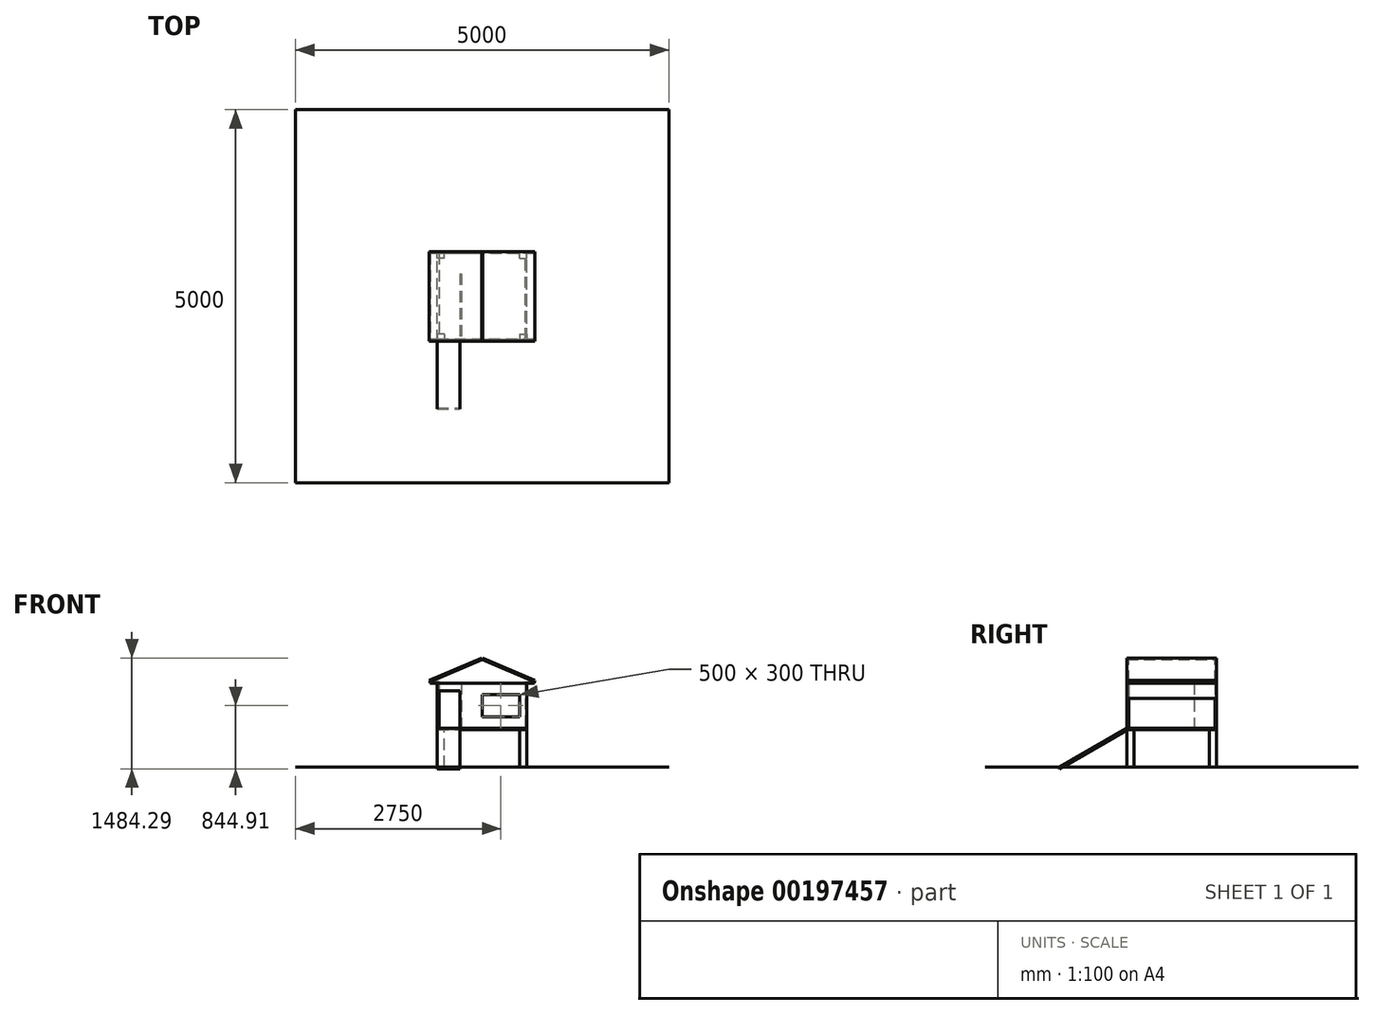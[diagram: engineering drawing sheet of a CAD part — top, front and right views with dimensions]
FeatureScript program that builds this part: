
annotation { "Feature Type Name" : "Feature", "Feature Type Description" : "" }
export const myFeature = defineFeature(function(context is Context, id is Id, definition is map)
    precondition{}
    {
        {
            var Q0;
            Q0=qCreatedBy(makeId("Top.planeOp"),FACE);
            var sketch = newSketch(context, id + "F0", { "sketchPlane" : qUnion([Q0])});
            skLineSegment(sketch, "E0.bottom", {"start": v(2500, -2500) * mm, "end": v(-2500, -2500) * mm});
            skLineSegment(sketch, "E0.top", {"start": v(2500, 2500) * mm, "end": v(-2500, 2500) * mm});
            skLineSegment(sketch, "E0.left", {"start": v(2500, -2500) * mm, "end": v(2500, 2500) * mm});
            skLineSegment(sketch, "E0.right", {"start": v(-2500, -2500) * mm, "end": v(-2500, 2500) * mm});
            skPoint(sketch, "E0.middle", {"position": v(0, 0) * mm});
            skSolve(sketch);
        }
        {
            var Q0;
            Q0 = qSketchRegion(id + "F0", true);
            extrude(context, id + "F1", {"entities" : qUnion([Q0]), "oppositeDirection" : true, "depth" : 1 * mm});
        }
        {
            var Q0;
            Q0=qCreatedBy(makeId("Top.planeOp"),FACE);
            cPlane(context, id + "F2", {"entities" : qUnion([Q0]), "cplaneType" : CPlaneType.OFFSET, "offset" : 500 * mm, "width" : 150 * mm, "height" : 150 * mm});
        }
        {
            var Q0;
            Q0=qCreatedBy(id+"F2.planeOp",FACE);
            var sketch = newSketch(context, id + "F3", { "sketchPlane" : qUnion([Q0])});
            skLineSegment(sketch, "E1.bottom", {"start": v(600, -600) * mm, "end": v(-600, -600) * mm});
            skLineSegment(sketch, "E1.top", {"start": v(600, 600) * mm, "end": v(-600, 600) * mm});
            skLineSegment(sketch, "E1.left", {"start": v(600, -600) * mm, "end": v(600, 600) * mm});
            skLineSegment(sketch, "E1.right", {"start": v(-600, -600) * mm, "end": v(-600, 600) * mm});
            skPoint(sketch, "E1.middle", {"position": v(0, 0) * mm});
            skSolve(sketch);
        }
        {
            var Q0;
            Q0 = qSketchRegion(id + "F3", true);
            extrude(context, id + "F4", {"entities" : qUnion([Q0]), "depth" : 22 * mm});
        }
        {
            var Q0;
            Q0=qCreatedBy(id+"F2.planeOp",FACE);
            var sketch = newSketch(context, id + "F5", { "sketchPlane" : qUnion([Q0])});
            skLineSegment(sketch, "E2.bottom", {"start": v(-600, 600) * mm, "end": v(-505, 600) * mm});
            skLineSegment(sketch, "E2.top", {"start": v(-600, 505) * mm, "end": v(-505, 505) * mm});
            skLineSegment(sketch, "E2.left", {"start": v(-600, 600) * mm, "end": v(-600, 505) * mm});
            skLineSegment(sketch, "E2.right", {"start": v(-505, 600) * mm, "end": v(-505, 505) * mm});
            skLineSegment(sketch, "E3", {"start": v(0, 0) * mm, "end": v(0, 720.23) * mm, "construction": true});
            skLineSegment(sketch, "E4", {"start": v(-681.79, 0) * mm, "end": v(744.72, 0) * mm, "construction": true});
            skLineSegment(sketch, "E5.MirrorCS", {"start": v(505, 600) * mm, "end": v(505, 505) * mm});
            skLineSegment(sketch, "E6.MirrorCS", {"start": v(600, 600) * mm, "end": v(600, 505) * mm});
            skLineSegment(sketch, "E7.MirrorCS", {"start": v(600, 505) * mm, "end": v(505, 505) * mm});
            skLineSegment(sketch, "E8.MirrorCS", {"start": v(600, 600) * mm, "end": v(505, 600) * mm});
            skLineSegment(sketch, "E9.MirrorCS", {"start": v(-505, -600) * mm, "end": v(-505, -505) * mm});
            skLineSegment(sketch, "E10.MirrorCS", {"start": v(-600, -600) * mm, "end": v(-600, -505) * mm});
            skLineSegment(sketch, "E11.MirrorCS", {"start": v(-600, -505) * mm, "end": v(-505, -505) * mm});
            skLineSegment(sketch, "E12.MirrorCS", {"start": v(-600, -600) * mm, "end": v(-505, -600) * mm});
            skLineSegment(sketch, "E13.MirrorCS", {"start": v(505, -600) * mm, "end": v(505, -505) * mm});
            skLineSegment(sketch, "E14.MirrorCS", {"start": v(600, -600) * mm, "end": v(600, -505) * mm});
            skLineSegment(sketch, "E15.MirrorCS", {"start": v(600, -505) * mm, "end": v(505, -505) * mm});
            skLineSegment(sketch, "E16.MirrorCS", {"start": v(600, -600) * mm, "end": v(505, -600) * mm});
            skSolve(sketch);
        }
        {
            var Q0;
            Q0 = qSketchRegion(id + "F5", true);
            extrude(context, id + "F6", {"entities" : qUnion([Q0]), "endBound" : BoundingType.UP_TO_NEXT, "oppositeDirection" : true, "depth" : 25 * mm});
        }
        {
            var Q0;
            Q0=makeQuery(id+"F4.opExtrude","CAP_FACE",FACE,{"disambiguationData":[OSD([sQuery(id+"F3.wireOp",EDGE,"E1.bottom"),sQuery(id+"F3.wireOp",EDGE,"E1.top"),sQuery(id+"F3.wireOp",EDGE,"E1.left"),sQuery(id+"F3.wireOp",EDGE,"E1.right")])],"isStart":false});
            var sketch = newSketch(context, id + "F7", { "sketchPlane" : qUnion([Q0])});
            skLineSegment(sketch, "E17.bottom", {"start": v(-600, 600) * mm, "end": v(600, 600) * mm});
            skLineSegment(sketch, "E17.top", {"start": v(-600, -600) * mm, "end": v(600, -600) * mm});
            skLineSegment(sketch, "E17.left", {"start": v(-600, 600) * mm, "end": v(-600, -600) * mm});
            skLineSegment(sketch, "E17.right", {"start": v(600, 600) * mm, "end": v(600, -600) * mm});
            skLineSegment(sketch, "E18.0", {"start": v(-578, 578) * mm, "end": v(578, 578) * mm});
            skLineSegment(sketch, "E18.1", {"start": v(-578, 578) * mm, "end": v(-578, -578) * mm});
            skLineSegment(sketch, "E18.2", {"start": v(-578, -578) * mm, "end": v(578, -578) * mm});
            skLineSegment(sketch, "E18.3", {"start": v(578, 578) * mm, "end": v(578, -578) * mm});
            skSolve(sketch);
        }
        {
            var Q0;
            Q0 = qSketchRegion(id + "F7", true);
            extrude(context, id + "F8", {"entities" : qUnion([Q0]), "depth" : 600 * mm});
        }
        {
            var Q0;
            Q0=makeQuery(id+"F4.opExtrude","CAP_EDGE",EDGE,{"disambiguationData":[OSD([sQuery(id+"F3.wireOp",EDGE,"E1.bottom")])],"isStart":false});
            cPlane(context, id + "F9", {"entities" : qUnion([Q0]), "cplaneType" : CPlaneType.LINE_ANGLE, "offset" : 25 * mm, "angle" : 60 * degree, "width" : 150 * mm, "height" : 150 * mm});
        }
        {
            var Q0;
            Q0=qCreatedBy(id+"F9.planeOp",FACE);
            var sketch = newSketch(context, id + "F10", { "sketchPlane" : qUnion([Q0])});
            skLineSegment(sketch, "E19.bottom", {"start": v(-600, -258.62) * mm, "end": v(-300, -258.62) * mm});
            skLineSegment(sketch, "E19.top", {"start": v(-600, -1310.34) * mm, "end": v(-300, -1310.34) * mm});
            skLineSegment(sketch, "E19.left", {"start": v(-600, -258.62) * mm, "end": v(-600, -1310.34) * mm});
            skLineSegment(sketch, "E19.right", {"start": v(-300, -258.62) * mm, "end": v(-300, -1310.34) * mm});
            skSolve(sketch);
        }
        {
            var Q0;
            Q0 = qSketchRegion(id + "F10", true);
            extrude(context, id + "F11", {"entities" : qUnion([Q0]), "oppositeDirection" : true, "depth" : 22 * mm});
        }
        {
            var Q0;
            Q0=makeQuery(id+"F4.opExtrude","CAP_FACE",FACE,{"disambiguationData":[OSD([sQuery(id+"F3.wireOp",EDGE,"E1.bottom"),sQuery(id+"F3.wireOp",EDGE,"E1.top"),sQuery(id+"F3.wireOp",EDGE,"E1.left"),sQuery(id+"F3.wireOp",EDGE,"E1.right")])],"isStart":false});
            var sketch = newSketch(context, id + "F12", { "sketchPlane" : qUnion([Q0])});
            skLineSegment(sketch, "E20.bottom", {"start": v(-300, 300) * mm, "end": v(-278, 300) * mm});
            skLineSegment(sketch, "E20.top", {"start": v(-300, -578) * mm, "end": v(-278, -578) * mm});
            skLineSegment(sketch, "E20.left", {"start": v(-300, 300) * mm, "end": v(-300, -578) * mm});
            skLineSegment(sketch, "E20.right", {"start": v(-278, 300) * mm, "end": v(-278, -578) * mm});
            skSolve(sketch);
        }
        {
            var Q0;
            Q0 = qSketchRegion(id + "F12", true);
            extrude(context, id + "F13", {"entities" : qUnion([Q0]), "depth" : 600 * mm});
        }
        {
            var Q0;
            Q0=makeQuery(id+"F8.opExtrude","SWEPT_FACE",FACE,{"disambiguationData":[OSD([sQuery(id+"F7.wireOp",EDGE,"E17.top")])]});
            var sketch = newSketch(context, id + "F14", { "sketchPlane" : qUnion([Q0])});
            skLineSegment(sketch, "E21.bottom", {"start": v(-578, 1022) * mm, "end": v(-300, 1022) * mm});
            skLineSegment(sketch, "E21.top", {"start": v(-578, 522) * mm, "end": v(-300, 522) * mm});
            skLineSegment(sketch, "E21.left", {"start": v(-578, 1022) * mm, "end": v(-578, 522) * mm});
            skLineSegment(sketch, "E21.right", {"start": v(-300, 1022) * mm, "end": v(-300, 522) * mm});
            skSolve(sketch);
        }
        {
            var Q0;
            Q0 = qSketchRegion(id + "F14", true);
            extrude(context, id + "F15", {"entities" : qUnion([Q0]), "operationType" : NewBodyOperationType.REMOVE, "endBound" : BoundingType.UP_TO_NEXT, "oppositeDirection" : true, "depth" : 25 * mm});
        }
        {
            var Q0;
            Q0=makeQuery(id+"F8.opExtrude","SWEPT_FACE",FACE,{"disambiguationData":[OSD([sQuery(id+"F7.wireOp",EDGE,"E17.right")])]});
            var sketch = newSketch(context, id + "F16", { "sketchPlane" : qUnion([Q0])});
            skLineSegment(sketch, "E22.bottom", {"start": v(-578, 922) * mm, "end": v(578, 922) * mm});
            skLineSegment(sketch, "E22.top", {"start": v(-578, 522) * mm, "end": v(578, 522) * mm});
            skLineSegment(sketch, "E22.left", {"start": v(-578, 922) * mm, "end": v(-578, 522) * mm});
            skLineSegment(sketch, "E22.right", {"start": v(578, 922) * mm, "end": v(578, 522) * mm});
            skSolve(sketch);
        }
        {
            var Q0;
            Q0 = qSketchRegion(id + "F16", true);
            extrude(context, id + "F17", {"entities" : qUnion([Q0]), "operationType" : NewBodyOperationType.REMOVE, "endBound" : BoundingType.UP_TO_NEXT, "oppositeDirection" : true, "depth" : 25 * mm});
        }
        {
            var Q0;
            Q0=makeQuery(id+"F8.opExtrude","SWEPT_FACE",FACE,{"disambiguationData":[OSD([sQuery(id+"F7.wireOp",EDGE,"E17.right")])]});
            var sketch = newSketch(context, id + "F18", { "sketchPlane" : qUnion([Q0])});
            skLineSegment(sketch, "E23.bottom", {"start": v(-578, 922) * mm, "end": v(578, 922) * mm});
            skLineSegment(sketch, "E23.top", {"start": v(-578, 522) * mm, "end": v(578, 522) * mm});
            skLineSegment(sketch, "E23.left", {"start": v(-578, 922) * mm, "end": v(-578, 522) * mm});
            skLineSegment(sketch, "E23.right", {"start": v(578, 922) * mm, "end": v(578, 522) * mm});
            skSolve(sketch);
        }
        {
            var Q0;
            Q0 = qSketchRegion(id + "F18", true);
            extrude(context, id + "F19", {"entities" : qUnion([Q0]), "oppositeDirection" : true, "depth" : 22 * mm});
        }
        {
            var Q0;
            Q0=makeQuery(id+"F8.opExtrude","SWEPT_FACE",FACE,{"disambiguationData":[OSD([sQuery(id+"F7.wireOp",EDGE,"E17.top")])]});
            var sketch = newSketch(context, id + "F20", { "sketchPlane" : qUnion([Q0])});
            skLineSegment(sketch, "E24.bottom", {"start": v(0, 972) * mm, "end": v(500, 972) * mm});
            skLineSegment(sketch, "E24.top", {"start": v(0, 672) * mm, "end": v(500, 672) * mm});
            skLineSegment(sketch, "E24.left", {"start": v(0, 972) * mm, "end": v(0, 672) * mm});
            skLineSegment(sketch, "E24.right", {"start": v(500, 972) * mm, "end": v(500, 672) * mm});
            skSolve(sketch);
        }
        {
            var Q0;
            Q0 = qSketchRegion(id + "F20", true);
            extrude(context, id + "F21", {"entities" : qUnion([Q0]), "operationType" : NewBodyOperationType.REMOVE, "endBound" : BoundingType.UP_TO_NEXT, "oppositeDirection" : true, "depth" : 25 * mm});
        }
        {
            var Q0;
            Q0=makeQuery(id+"F8.opExtrude","SWEPT_FACE",FACE,{"disambiguationData":[OSD([sQuery(id+"F7.wireOp",EDGE,"E17.top")])]});
            var sketch = newSketch(context, id + "F22", { "sketchPlane" : qUnion([Q0])});
            skLineSegment(sketch, "E25", {"start": v(0, 0) * mm, "end": v(0, 1688.78) * mm, "construction": true});
            skLineSegment(sketch, "E26", {"start": v(-700, 1122) * mm, "end": v(700, 1122) * mm});
            skLineSegment(sketch, "E27", {"start": v(-700, 1122) * mm, "end": v(-700, 1144) * mm});
            skLineSegment(sketch, "E28", {"start": v(-700, 1144) * mm, "end": v(0, 1441.13) * mm});
            skLineSegment(sketch, "E29", {"start": v(700, 1122) * mm, "end": v(700, 1144) * mm});
            skLineSegment(sketch, "E30", {"start": v(700, 1144) * mm, "end": v(0, 1441.13) * mm});
            skSolve(sketch);
        }
        {
            var Q0;
            Q0 = qSketchRegion(id + "F22", true);
            extrude(context, id + "F23", {"entities" : qUnion([Q0]), "oppositeDirection" : true, "depth" : 22 * mm});
        }
        {
            var Q0;
            Q0=makeQuery(id+"F23.opExtrude","SWEPT_BODY",BODY,{"disambiguationData":[OSD([sQuery(id+"F22.wireOp",EDGE,"E26"),sQuery(id+"F22.wireOp",EDGE,"lWtLeS8S-gMhO-y6JL-Wjuz-mZaUUvy0QFBU"),sQuery(id+"F22.wireOp",EDGE,"m84qWRCe-eZef-hMwX-0Vxn-EiRq6ELt9xTd")])]});
            var Q1;
            Q1=qCreatedBy(makeId("Front.planeOp"),FACE);
            mirror(context, id + "F24", {"entities" : qUnion([Q0]), "mirrorPlane" : qUnion([Q1])});
        }
        {
            var Q0;
            Q0=makeQuery(id+"F8.opExtrude","CAP_FACE",FACE,{"disambiguationData":[OSD([sQuery(id+"F7.wireOp",EDGE,"E17.bottom"),sQuery(id+"F7.wireOp",EDGE,"E17.top"),sQuery(id+"F7.wireOp",EDGE,"E17.left"),sQuery(id+"F7.wireOp",EDGE,"E17.right"),sQuery(id+"F7.wireOp",EDGE,"E18.0"),sQuery(id+"F7.wireOp",EDGE,"E18.1"),sQuery(id+"F7.wireOp",EDGE,"E18.2"),sQuery(id+"F7.wireOp",EDGE,"E18.3")])],"isStart":false});
            var sketch = newSketch(context, id + "F25", { "sketchPlane" : qUnion([Q0])});
            skLineSegment(sketch, "E31.bottom", {"start": v(-578, 578) * mm, "end": v(-700, 578) * mm});
            skLineSegment(sketch, "E31.top", {"start": v(-578, -578) * mm, "end": v(-700, -578) * mm});
            skLineSegment(sketch, "E31.left", {"start": v(-578, 578) * mm, "end": v(-578, -578) * mm});
            skLineSegment(sketch, "E31.right", {"start": v(-700, 578) * mm, "end": v(-700, -578) * mm});
            skSolve(sketch);
        }
        {
            var Q0;
            Q0 = qSketchRegion(id + "F25", true);
            extrude(context, id + "F26", {"entities" : qUnion([Q0]), "depth" : 22 * mm});
        }
        {
            var Q0;
            Q0=makeQuery(id+"F26.opExtrude","SWEPT_BODY",BODY,{"disambiguationData":[OSD([sQuery(id+"F25.wireOp",EDGE,"E31.bottom"),sQuery(id+"F25.wireOp",EDGE,"E31.top"),sQuery(id+"F25.wireOp",EDGE,"E31.left"),sQuery(id+"F25.wireOp",EDGE,"E31.right")])]});
            var Q1;
            Q1=qCreatedBy(makeId("Right.planeOp"),FACE);
            mirror(context, id + "F27", {"entities" : qUnion([Q0]), "mirrorPlane" : qUnion([Q1])});
        }
        {
            var Q0;
            Q0=makeQuery(id+"F24.opPattern","COPY",FACE,{"derivedFrom":makeQuery(id+"F23.opExtrude","SWEPT_FACE",FACE,{"disambiguationData":[OSD([sQuery(id+"F22.wireOp",EDGE,"E28")])]}),"instanceName":"1"});
            var sketch = newSketch(context, id + "F28", { "sketchPlane" : qUnion([Q0])});
            skLineSegment(sketch, "E32.bottom", {"start": v(563.1, 600) * mm, "end": v(-197.36, 600) * mm});
            skLineSegment(sketch, "E32.top", {"start": v(563.1, -600) * mm, "end": v(-197.36, -600) * mm});
            skLineSegment(sketch, "E32.left", {"start": v(563.1, 600) * mm, "end": v(563.1, -600) * mm});
            skLineSegment(sketch, "E32.right", {"start": v(-197.36, 600) * mm, "end": v(-197.36, -600) * mm});
            skSolve(sketch);
        }
        {
            var Q0;
            Q0 = qSketchRegion(id + "F28", true);
            extrude(context, id + "F29", {"entities" : qUnion([Q0]), "depth" : 22 * mm});
        }
        {
            var Q0;
            Q0=makeQuery(id+"F29.opExtrude","SWEPT_BODY",BODY,{"disambiguationData":[OSD([sQuery(id+"F28.wireOp",EDGE,"E32.bottom"),sQuery(id+"F28.wireOp",EDGE,"E32.top"),sQuery(id+"F28.wireOp",EDGE,"E32.left"),sQuery(id+"F28.wireOp",EDGE,"E32.right")])]});
            var Q1;
            Q1=qCreatedBy(makeId("Right.planeOp"),FACE);
            mirror(context, id + "F30", {"entities" : qUnion([Q0]), "mirrorPlane" : qUnion([Q1])});
        }
    });
